# Revit family: IRIS-PS-BB 4500-8xx-xx-O-EDx3
name_source: partatom
category: Oprawy oświetleniowe
revit_build: Autodesk Revit 2017 (Build: 20190507_1515(x64)
units: mm (PartAtom-declared; Revit-internal decimal feet)

## family parameters
Numer OmniClass = 23.80.70.11
Obiekt nadrzędny = Powierzchnia
Punkt obliczania pomieszczeń = Nie
Tnij formami wycięć po wczytaniu = Nie
Typ części = Normalny
Tytuł OmniClass = Luminaries for Internal Lighting
Współdzielony = Nie
Wymiar okrągłego złącza = Użyj średnicy
Źródło światła = Tak

## types (8) — shared parameters
Emituj kształt widoczny w renderingu = Nie
Emituj ze średnicy okręgu = 375 mm  [stored 1.23031 ft]
Filtr koloru = 16777215
Kod zespołu = D5020200
Lampa = LED
Obciążenie pozorne = 33 VA
Odchylenie kierunku = 90.00°
Plik sieci fotometrycznej = IRIS-PS 4500-840-ND-O.IES
Producent = RIDI Leuchten GmbH
URL = www.spectral-lighting.com
Zmiana temperatury barwowej przyciemniania lampy = <Brak>
brand = Spectral
conformity mark = CE
electrical safety class = 1
height = 50 mm  [stored 0.164042 ft]
ingress protection (IP) code = IP20
length = 375 mm  [stored 1.23031 ft]
nominal frequency = 50-60Hz
nominal voltage = 230
rated input power = 33
voltage type (AC, DC, UC) = AC
weight = 2.0 kg
width = 375 mm  [stored 1.23031 ft]
zero-valued in all types: Domyślna rzędna

## per-type parameters (varying)
| type | Model |
| IRIS-PS-BB 4500-830-ND-O-EDS3 | SPI0000238//342 |
| IRIS-PS-BB 4500-840-ND-O-EDS3 | SPI0000239//342 |
| IRIS-PS-BB 4500-830-DA-O-EDS3 | SPI0000240//342 |
| IRIS-PS-BB 4500-840-DA-O-EDS3 | SPI0000241//342 |
| IRIS-PS-BB 4500-8TW-DA-O-EDS3 | SPI0000242//342 |
| IRIS-PS-BB 4500-830-DA-O-EDP3 | SPI0000240//344 |
| IRIS-PS-BB 4500-840-DA-O-EDP3 | SPI0000241//344 |
| IRIS-PS-BB 4500-8TW-DA-O-EDP3 | SPI0000242//344 |

note: column(s) folded — value = type name in every type: product name

note: [stored X ft] marks values corroborated as IEEE doubles in the binary element streams (Revit-internal decimal feet)
